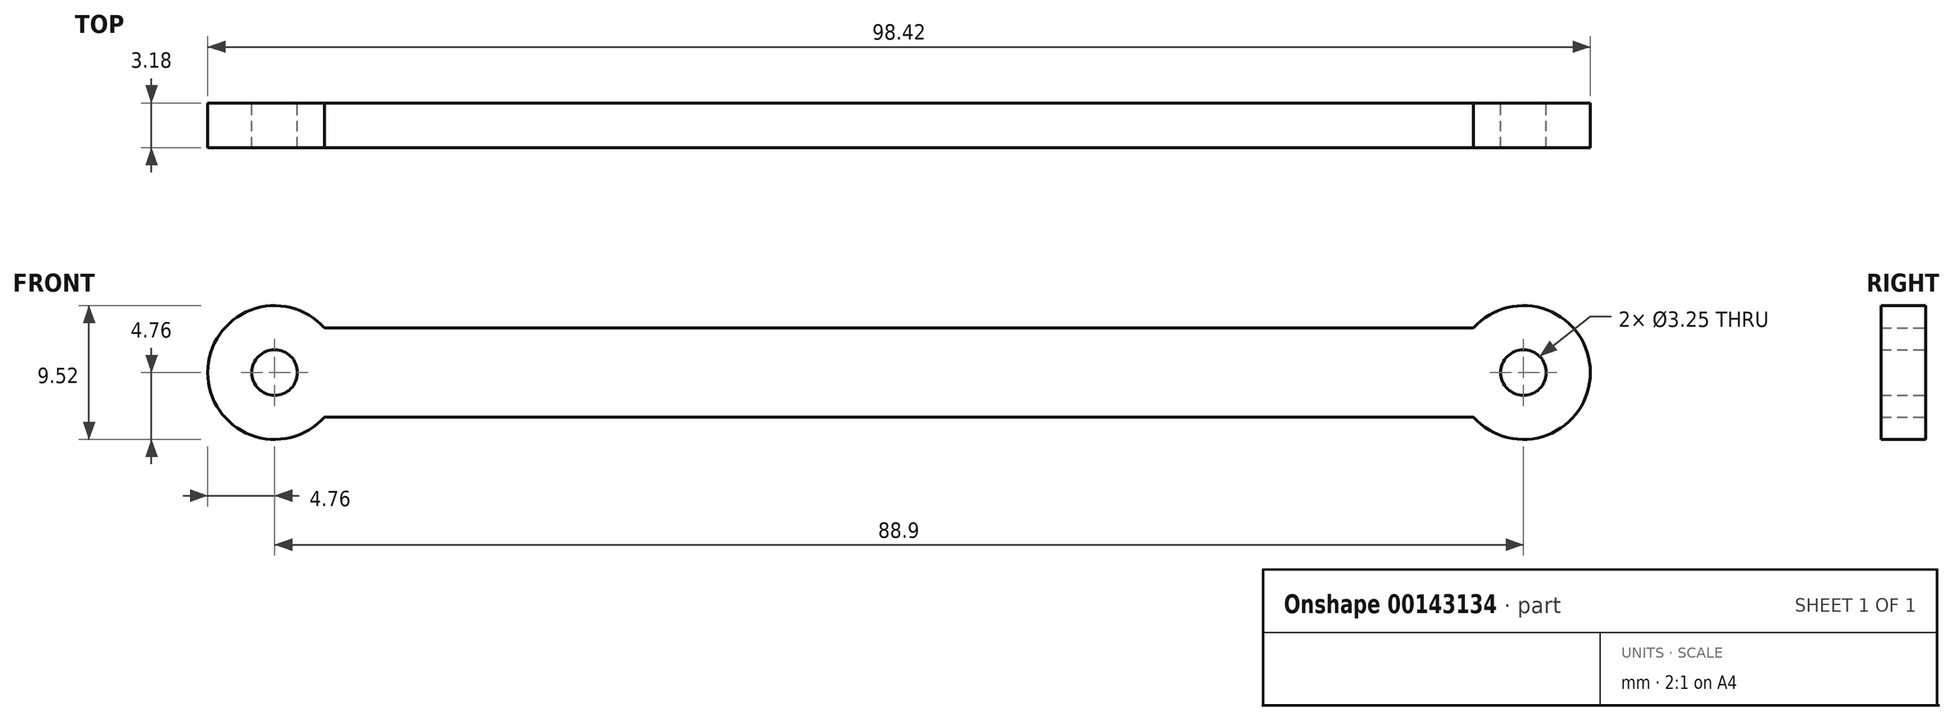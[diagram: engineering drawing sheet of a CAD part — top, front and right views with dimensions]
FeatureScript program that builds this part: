
annotation { "Feature Type Name" : "Feature", "Feature Type Description" : "" }
export const myFeature = defineFeature(function(context is Context, id is Id, definition is map)
    precondition{}
    {
        {
            var Q0;
            Q0=qCreatedBy(makeId("Front.planeOp"),FACE);
            var sketch = newSketch(context, id + "F0", { "sketchPlane" : qUnion([Q0])});
            skArc(sketch, "E0", {"start": v(3.55, 3.18) * mm, "mid": v(-4.76, 0) * mm, "end": v(3.55, -3.18) * mm});
            skArc(sketch, "E1", {"start": v(85.35, -3.17) * mm, "mid": v(93.66, 0) * mm, "end": v(85.35, 3.18) * mm});
            skLineSegment(sketch, "E2.bottom", {"start": v(3.55, 3.18) * mm, "end": v(85.35, 3.18) * mm});
            skLineSegment(sketch, "E2.top", {"start": v(3.55, -3.18) * mm, "end": v(85.35, -3.18) * mm});
            skPoint(sketch, "E3.orphan", {"position": v(0, 3.18) * mm});
            skCircle(sketch, "E4", {"center": v(0, 0) * mm, "radius": 1.63 * mm});
            skCircle(sketch, "E5", {"center": v(88.9, 0) * mm, "radius": 1.63 * mm});
            skSolve(sketch);
        }
        {
            var Q0;
            Q0=makeQuery(id+"F0.imprint","IMPRINT",FACE,{"disambiguationData":[TD([[makeQuery(id+"F0.imprint","IMPRINT",EDGE,{"derivedFrom":sQuery(id+"F0.wireOp",EDGE,"E0")}),1.0]])]});
            extrude(context, id + "F1", {"entities" : qUnion([Q0]), "depth" : 3.17 * mm});
        }
    });
